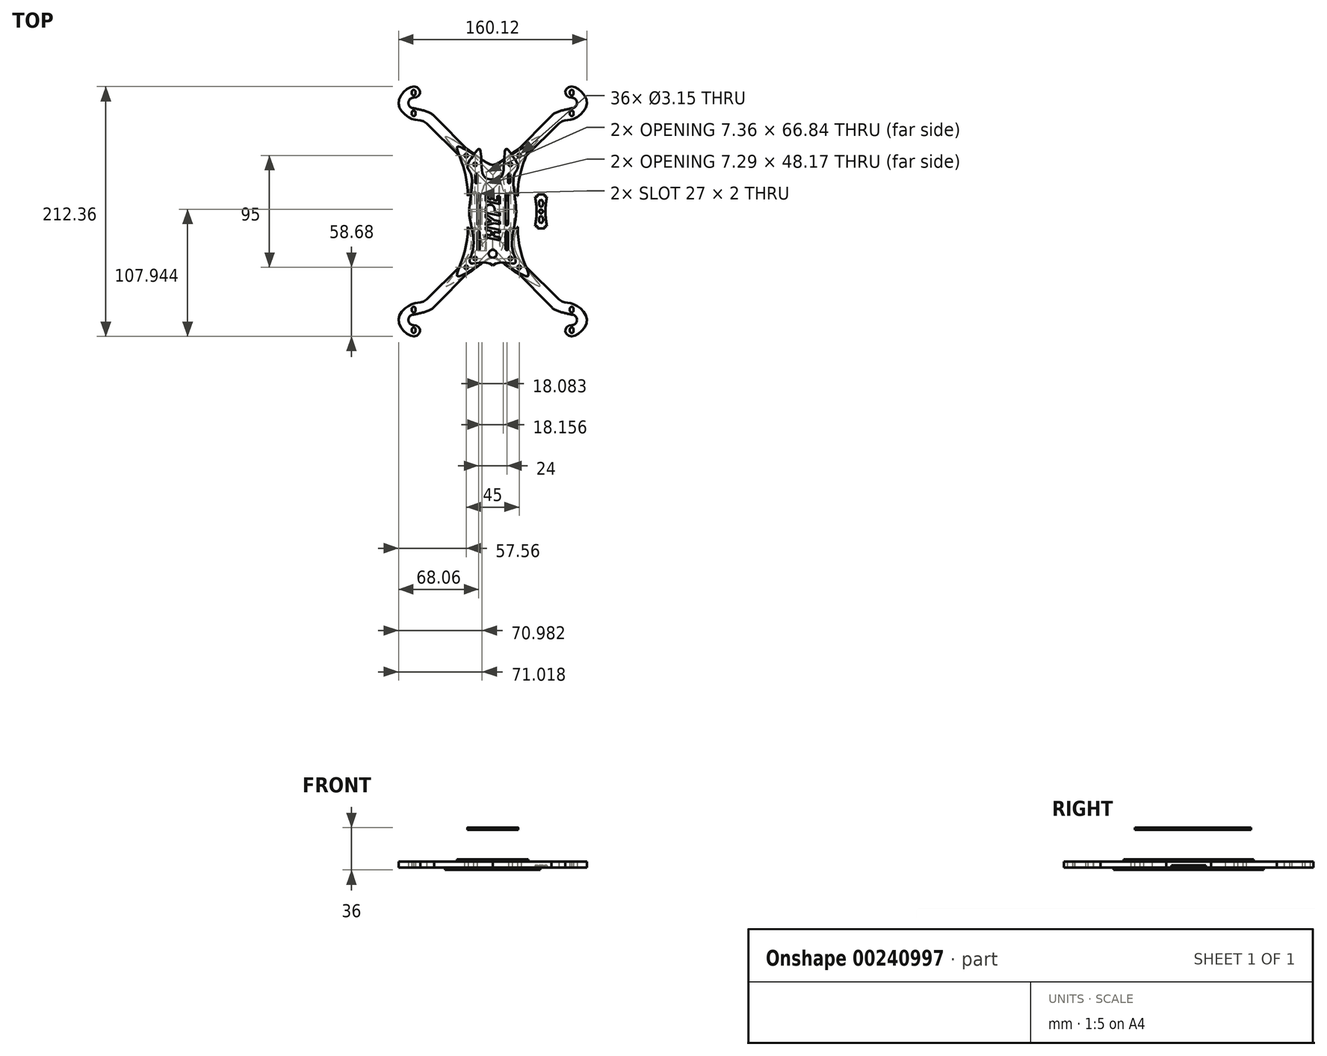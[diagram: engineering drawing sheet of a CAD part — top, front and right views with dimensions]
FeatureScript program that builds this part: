
annotation { "Feature Type Name" : "Feature", "Feature Type Description" : "" }
export const myFeature = defineFeature(function(context is Context, id is Id, definition is map)
    precondition{}
    {
        {
            var Q0;
            Q0=qCreatedBy(makeId("Top.planeOp"),FACE);
            var sketch = newSketch(context, id + "F0", { "sketchPlane" : qUnion([Q0])});
            skLineSegment(sketch, "E0.bottom", {"start": v(15.25, 15.25) * mm, "end": v(-15.25, 15.25) * mm, "construction": true});
            skLineSegment(sketch, "E0.top", {"start": v(15.25, -15.25) * mm, "end": v(-15.25, -15.25) * mm, "construction": true});
            skLineSegment(sketch, "E0.left", {"start": v(15.25, 15.25) * mm, "end": v(15.25, -15.25) * mm, "construction": true});
            skLineSegment(sketch, "E0.right", {"start": v(-15.25, 15.25) * mm, "end": v(-15.25, -15.25) * mm, "construction": true});
            skPoint(sketch, "E0.middle", {"position": v(0, 0) * mm});
            skCircle(sketch, "E1", {"center": v(15.25, 15.25) * mm, "radius": 1.57 * mm});
            skCircle(sketch, "E2", {"center": v(-15.25, 15.25) * mm, "radius": 1.57 * mm});
            skCircle(sketch, "E3", {"center": v(-15.25, -15.25) * mm, "radius": 1.57 * mm});
            skCircle(sketch, "E4", {"center": v(15.25, -15.25) * mm, "radius": 1.57 * mm});
            skLineSegment(sketch, "E5", {"start": v(0, 25) * mm, "end": v(0, -25) * mm, "construction": true});
            skLineSegment(sketch, "E6", {"start": v(0, 25) * mm, "end": v(67.18, 92.18) * mm, "construction": true});
            skLineSegment(sketch, "E7", {"start": v(-57.6, 0) * mm, "end": v(85.6, 0) * mm, "construction": true});
            skLineSegment(sketch, "E8.MirrorCS", {"start": v(0, -25) * mm, "end": v(67.18, -92.18) * mm, "construction": true});
            skLineSegment(sketch, "E9.MirrorCS", {"start": v(0, 25) * mm, "end": v(-67.18, 92.18) * mm, "construction": true});
            skLineSegment(sketch, "E10.MirrorCS", {"start": v(0, -25) * mm, "end": v(-67.18, -92.18) * mm, "construction": true});
            skCircle(sketch, "E11", {"center": v(67.18, 92.18) * mm, "radius": 64.77 * mm, "construction": true});
            skCircle(sketch, "E12", {"center": v(-67.18, 92.18) * mm, "radius": 64.77 * mm, "construction": true});
            skCircle(sketch, "E13", {"center": v(-67.18, -92.18) * mm, "radius": 64.77 * mm, "construction": true});
            skCircle(sketch, "E14", {"center": v(67.18, -92.18) * mm, "radius": 64.77 * mm, "construction": true});
            skLineSegment(sketch, "E15.bottom", {"start": v(18, 18) * mm, "end": v(-18, 18) * mm, "construction": true});
            skLineSegment(sketch, "E15.top", {"start": v(18, -18) * mm, "end": v(-18, -18) * mm, "construction": true});
            skLineSegment(sketch, "E15.left", {"start": v(18, 18) * mm, "end": v(18, -18) * mm, "construction": true});
            skLineSegment(sketch, "E15.right", {"start": v(-18, 18) * mm, "end": v(-18, -18) * mm, "construction": true});
            skSolve(sketch);
        }
        {
            var Q0;
            Q0=qCreatedBy(makeId("Top.planeOp"),FACE);
            var sketch = newSketch(context, id + "F1", { "sketchPlane" : qUnion([Q0])});
            skLineSegment(sketch, "E16.0", {"start": v(0, 25) * mm, "end": v(67.18, 92.18) * mm, "construction": true});
            skLineSegment(sketch, "E16.1", {"start": v(0, 25) * mm, "end": v(-67.18, 92.18) * mm, "construction": true});
            skLineSegment(sketch, "E16.2", {"start": v(0, 25) * mm, "end": v(0, -25) * mm, "construction": true});
            skLineSegment(sketch, "E16.3", {"start": v(0, -25) * mm, "end": v(67.18, -92.18) * mm, "construction": true});
            skLineSegment(sketch, "E16.4", {"start": v(0, -25) * mm, "end": v(-67.18, -92.18) * mm, "construction": true});
            skCircle(sketch, "E17", {"center": v(67.18, 92.18) * mm, "radius": 9.5 * mm, "construction": true});
            skCircle(sketch, "E18", {"center": v(67.18, 92.18) * mm, "radius": 8 * mm, "construction": true});
            skArc(sketch, "E19", {"start": v(67.18, 87.68) * mm, "mid": v(71.68, 92.18) * mm, "end": v(67.18, 96.68) * mm});
            skCircle(sketch, "E20", {"center": v(67.18, 92.18) * mm, "radius": 14 * mm, "construction": true});
            skLineSegment(sketch, "E21", {"start": v(67.18, 92.18) * mm, "end": v(85, 110) * mm, "construction": true});
            skLineSegment(sketch, "E22", {"start": v(52.08, 107.27) * mm, "end": v(67.18, 92.18) * mm, "construction": true});
            skLineSegment(sketch, "E23", {"start": v(67.18, 92.18) * mm, "end": v(82.27, 77.08) * mm, "construction": true});
            skLineSegment(sketch, "E24", {"start": v(67.18, 67.97) * mm, "end": v(67.18, 92.18) * mm, "construction": true});
            skLineSegment(sketch, "E25", {"start": v(67.18, 115.7) * mm, "end": v(67.18, 92.18) * mm, "construction": true});
            skLineSegment(sketch, "E26", {"start": v(42.73, 92.18) * mm, "end": v(67.18, 92.18) * mm, "construction": true});
            skLineSegment(sketch, "E27", {"start": v(96.59, 92.18) * mm, "end": v(67.18, 92.18) * mm, "construction": true});
            skLineSegment(sketch, "E28", {"start": v(67.18, 100.18) * mm, "end": v(67.18, 101.68) * mm, "construction": true});
            skArc(sketch, "E29.0.startCap", {"start": v(68.75, 100.18) * mm, "mid": v(67.18, 98.6) * mm, "end": v(65.6, 100.18) * mm});
            skArc(sketch, "E29.0.endCap", {"start": v(65.6, 101.68) * mm, "mid": v(67.18, 103.25) * mm, "end": v(68.75, 101.68) * mm});
            skLineSegment(sketch, "E29.0.left", {"start": v(65.6, 100.18) * mm, "end": v(65.6, 101.68) * mm});
            skLineSegment(sketch, "E29.0.right", {"start": v(68.75, 100.18) * mm, "end": v(68.75, 101.68) * mm});
            skLineSegment(sketch, "E30", {"start": v(49.85, 81.21) * mm, "end": v(53.03, 78.03) * mm, "construction": true});
            skLineSegment(sketch, "E31", {"start": v(53.03, 78.03) * mm, "end": v(56.21, 74.85) * mm, "construction": true});
            skLineSegment(sketch, "E32", {"start": v(0, 25) * mm, "end": v(0, 53.5) * mm, "construction": true});
            skLineSegment(sketch, "E33", {"start": v(0, -25) * mm, "end": v(0, -52.13) * mm, "construction": true});
            skPoint(sketch, "E34", {"position": v(67.18, 80.07) * mm});
            skLineSegment(sketch, "E35", {"start": v(0, 31) * mm, "end": v(0, 19) * mm});
            skArc(sketch, "E36.MirrorCS", {"start": v(65.6, 82.68) * mm, "mid": v(67.18, 81.1) * mm, "end": v(68.75, 82.68) * mm});
            skLineSegment(sketch, "E37.MirrorCS", {"start": v(68.75, 84.18) * mm, "end": v(68.75, 82.68) * mm});
            skLineSegment(sketch, "E38.MirrorCS", {"start": v(65.6, 84.18) * mm, "end": v(65.6, 82.68) * mm});
            skArc(sketch, "E39.MirrorCS", {"start": v(68.75, 84.18) * mm, "mid": v(67.18, 85.75) * mm, "end": v(65.6, 84.18) * mm});
            skFitSpline(sketch, "E40", {"points": [v(67.18, 87.68) * mm, v(49.85, 81.21) * mm], "startDerivative": vector(-16.97, -3.47) * mm, "endDerivative": vector(-9.2, -10.93) * mm});
            skFitSpline(sketch, "E41", {"points": [v(56.21, 74.85) * mm, v(67.18, 78.18) * mm, v(80.06, 92.18) * mm, v(67.18, 106.18) * mm, v(61.64, 101) * mm, v(67.18, 96.68) * mm], "startDerivative": vector(71.32, 56.31) * mm, "endDerivative": vector(56.06, 0.47) * mm});
            skPoint(sketch, "E42", {"position": v(81.88, 92.18) * mm});
            skLineSegment(sketch, "E43.MirrorCS", {"start": v(-67.18, 100.18) * mm, "end": v(-67.18, 101.68) * mm, "construction": true});
            skLineSegment(sketch, "E44.MirrorCS", {"start": v(-49.85, 81.21) * mm, "end": v(-53.03, 78.03) * mm, "construction": true});
            skLineSegment(sketch, "E45.MirrorCS", {"start": v(-53.03, 78.03) * mm, "end": v(-56.21, 74.85) * mm, "construction": true});
            skLineSegment(sketch, "E46.MirrorCS", {"start": v(-42.73, 92.18) * mm, "end": v(-67.18, 92.18) * mm, "construction": true});
            skLineSegment(sketch, "E47.MirrorCS", {"start": v(-67.18, 92.18) * mm, "end": v(-85, 110) * mm, "construction": true});
            skCircle(sketch, "E48.MirrorC", {"center": v(-67.18, 92.18) * mm, "radius": 14 * mm, "construction": true});
            skLineSegment(sketch, "E49.MirrorCS", {"start": v(-67.18, 67.97) * mm, "end": v(-67.18, 92.18) * mm, "construction": true});
            skLineSegment(sketch, "E50.MirrorCS", {"start": v(-67.18, 115.7) * mm, "end": v(-67.18, 92.18) * mm, "construction": true});
            skCircle(sketch, "E51.MirrorC", {"center": v(-67.18, 92.18) * mm, "radius": 8 * mm, "construction": true});
            skLineSegment(sketch, "E52.MirrorCS", {"start": v(-96.59, 92.18) * mm, "end": v(-67.18, 92.18) * mm, "construction": true});
            skCircle(sketch, "E53.MirrorC", {"center": v(-67.18, 92.18) * mm, "radius": 9.5 * mm, "construction": true});
            skPoint(sketch, "E54.MirrorP", {"position": v(-81.88, 92.18) * mm});
            skLineSegment(sketch, "E55.MirrorCS", {"start": v(-52.08, 107.27) * mm, "end": v(-67.18, 92.18) * mm, "construction": true});
            skLineSegment(sketch, "E56.MirrorCS", {"start": v(-67.18, 92.18) * mm, "end": v(-82.27, 77.08) * mm, "construction": true});
            skPoint(sketch, "E57.MirrorP", {"position": v(-67.18, 80.07) * mm});
            skLineSegment(sketch, "E58.MirrorCS", {"start": v(-67.18, -100.18) * mm, "end": v(-67.18, -101.68) * mm, "construction": true});
            skLineSegment(sketch, "E59.MirrorCS", {"start": v(53.03, -78.03) * mm, "end": v(56.21, -74.85) * mm, "construction": true});
            skLineSegment(sketch, "E60.MirrorCS", {"start": v(-53.03, -78.03) * mm, "end": v(-56.21, -74.85) * mm, "construction": true});
            skLineSegment(sketch, "E61.MirrorCS", {"start": v(-49.85, -81.21) * mm, "end": v(-53.03, -78.03) * mm, "construction": true});
            skLineSegment(sketch, "E62.MirrorCS", {"start": v(49.85, -81.21) * mm, "end": v(53.03, -78.03) * mm, "construction": true});
            skLineSegment(sketch, "E63.MirrorCS", {"start": v(67.18, -100.18) * mm, "end": v(67.18, -101.68) * mm, "construction": true});
            skLineSegment(sketch, "E64.MirrorCS", {"start": v(-52.08, -107.27) * mm, "end": v(-67.18, -92.18) * mm, "construction": true});
            skLineSegment(sketch, "E65.MirrorCS", {"start": v(67.18, -67.97) * mm, "end": v(67.18, -92.18) * mm, "construction": true});
            skLineSegment(sketch, "E66.MirrorCS", {"start": v(52.08, -107.27) * mm, "end": v(67.18, -92.18) * mm, "construction": true});
            skLineSegment(sketch, "E67.MirrorCS", {"start": v(-67.18, -92.18) * mm, "end": v(-82.27, -77.08) * mm, "construction": true});
            skLineSegment(sketch, "E68.MirrorCS", {"start": v(-67.18, -67.97) * mm, "end": v(-67.18, -92.18) * mm, "construction": true});
            skLineSegment(sketch, "E69.MirrorCS", {"start": v(42.73, -92.18) * mm, "end": v(67.18, -92.18) * mm, "construction": true});
            skLineSegment(sketch, "E70.MirrorCS", {"start": v(-67.18, -115.7) * mm, "end": v(-67.18, -92.18) * mm, "construction": true});
            skLineSegment(sketch, "E71.MirrorCS", {"start": v(-42.73, -92.18) * mm, "end": v(-67.18, -92.18) * mm, "construction": true});
            skLineSegment(sketch, "E72.MirrorCS", {"start": v(67.18, -115.7) * mm, "end": v(67.18, -92.18) * mm, "construction": true});
            skPoint(sketch, "E73.MirrorP", {"position": v(81.88, -92.18) * mm});
            skCircle(sketch, "E74.MirrorC", {"center": v(-67.18, -92.18) * mm, "radius": 8 * mm, "construction": true});
            skLineSegment(sketch, "E75.MirrorCS", {"start": v(67.18, -92.18) * mm, "end": v(82.27, -77.08) * mm, "construction": true});
            skLineSegment(sketch, "E76.MirrorCS", {"start": v(67.18, -92.18) * mm, "end": v(85, -110) * mm, "construction": true});
            skCircle(sketch, "E77.MirrorC", {"center": v(67.18, -92.18) * mm, "radius": 14 * mm, "construction": true});
            skCircle(sketch, "E78.MirrorC", {"center": v(67.18, -92.18) * mm, "radius": 8 * mm, "construction": true});
            skPoint(sketch, "E79.MirrorP", {"position": v(-81.88, -92.18) * mm});
            skPoint(sketch, "E80.MirrorP", {"position": v(67.18, -80.07) * mm});
            skLineSegment(sketch, "E81.MirrorCS", {"start": v(-67.18, -92.18) * mm, "end": v(-85, -110) * mm, "construction": true});
            skCircle(sketch, "E82.MirrorC", {"center": v(-67.18, -92.18) * mm, "radius": 14 * mm, "construction": true});
            skCircle(sketch, "E83.MirrorC", {"center": v(-67.18, -92.18) * mm, "radius": 9.5 * mm, "construction": true});
            skPoint(sketch, "E84.MirrorP", {"position": v(-67.18, -80.07) * mm});
            skLineSegment(sketch, "E85.MirrorCS", {"start": v(-96.59, -92.18) * mm, "end": v(-67.18, -92.18) * mm, "construction": true});
            skLineSegment(sketch, "E86.MirrorCS", {"start": v(96.59, -92.18) * mm, "end": v(67.18, -92.18) * mm, "construction": true});
            skCircle(sketch, "E87.MirrorC", {"center": v(67.18, -92.18) * mm, "radius": 9.5 * mm, "construction": true});
            skLineSegment(sketch, "E88.bottom", {"start": v(22.5, 47.5) * mm, "end": v(-22.5, 47.5) * mm, "construction": true});
            skLineSegment(sketch, "E88.top", {"start": v(22.5, -47.5) * mm, "end": v(-22.5, -47.5) * mm, "construction": true});
            skLineSegment(sketch, "E88.left", {"start": v(22.5, 47.5) * mm, "end": v(22.5, -47.5) * mm, "construction": true});
            skLineSegment(sketch, "E88.right", {"start": v(-22.5, 47.5) * mm, "end": v(-22.5, -47.5) * mm, "construction": true});
            skPoint(sketch, "E88.middle", {"position": v(0, 0) * mm});
            skLineSegment(sketch, "E89.bottom", {"start": v(15, 40) * mm, "end": v(-15, 40) * mm, "construction": true});
            skLineSegment(sketch, "E89.top", {"start": v(15, -40) * mm, "end": v(-15, -40) * mm, "construction": true});
            skLineSegment(sketch, "E89.left", {"start": v(15, 40) * mm, "end": v(15, -40) * mm, "construction": true});
            skLineSegment(sketch, "E89.right", {"start": v(-15, 40) * mm, "end": v(-15, -40) * mm, "construction": true});
            skCircle(sketch, "E90", {"center": v(22.5, 47.5) * mm, "radius": 1.57 * mm});
            skCircle(sketch, "E91", {"center": v(15, 40) * mm, "radius": 1.57 * mm});
            skCircle(sketch, "E92", {"center": v(-22.5, 47.5) * mm, "radius": 1.57 * mm, "construction": true});
            skCircle(sketch, "E93", {"center": v(-15, 40) * mm, "radius": 1.57 * mm, "construction": true});
            skCircle(sketch, "E94", {"center": v(22.5, -47.5) * mm, "radius": 1.57 * mm, "construction": true});
            skCircle(sketch, "E95", {"center": v(15, -40) * mm, "radius": 1.57 * mm, "construction": true});
            skCircle(sketch, "E96", {"center": v(-15, -40) * mm, "radius": 1.57 * mm, "construction": true});
            skCircle(sketch, "E97", {"center": v(-22.5, -47.5) * mm, "radius": 1.57 * mm, "construction": true});
            skLineSegment(sketch, "E98", {"start": v(49.85, 81.21) * mm, "end": v(0, 31) * mm});
            skLineSegment(sketch, "E99", {"start": v(56.21, 74.85) * mm, "end": v(0, 19) * mm});
            skSolve(sketch);
        }
        {
            var Q0;
            Q0 = qSketchRegion(id + "F1", true);
            extrude(context, id + "F2", {"entities" : qUnion([Q0]), "depth" : 5 * mm});
        }
        {
            var Q0;
            Q0=qCreatedBy(makeId("Top.planeOp"),FACE);
            cPlane(context, id + "F3", {"entities" : qUnion([Q0]), "cplaneType" : CPlaneType.OFFSET, "offset" : 5 * mm, "width" : 150 * mm, "height" : 150 * mm});
        }
        {
            var Q0;
            Q0=qCreatedBy(id+"F3.planeOp",FACE);
            var sketch = newSketch(context, id + "F4", { "sketchPlane" : qUnion([Q0])});
            skLineSegment(sketch, "E100", {"start": v(0, 93.49) * mm, "end": v(0, -92.27) * mm, "construction": true});
            skLineSegment(sketch, "E101", {"start": v(98.9, 0) * mm, "end": v(-102.09, 0) * mm, "construction": true});
            skCircle(sketch, "E102.0", {"center": v(22.5, 47.5) * mm, "radius": 1.57 * mm});
            skCircle(sketch, "E102.1", {"center": v(15, 40) * mm, "radius": 1.57 * mm});
            skCircle(sketch, "E102.2", {"center": v(-15, 40) * mm, "radius": 1.57 * mm});
            skCircle(sketch, "E102.3", {"center": v(-22.5, 47.5) * mm, "radius": 1.57 * mm});
            skCircle(sketch, "E102.4", {"center": v(15.25, 15.25) * mm, "radius": 1.57 * mm});
            skCircle(sketch, "E102.5", {"center": v(15.25, -15.25) * mm, "radius": 1.57 * mm});
            skCircle(sketch, "E102.6", {"center": v(-15.25, -15.25) * mm, "radius": 1.57 * mm});
            skCircle(sketch, "E102.7", {"center": v(-15.25, 15.25) * mm, "radius": 1.57 * mm});
            skCircle(sketch, "E102.8", {"center": v(15, -40) * mm, "radius": 1.57 * mm});
            skCircle(sketch, "E102.9", {"center": v(22.5, -47.5) * mm, "radius": 1.57 * mm});
            skCircle(sketch, "E102.10", {"center": v(-15, -40) * mm, "radius": 1.57 * mm});
            skCircle(sketch, "E102.11", {"center": v(-22.5, -47.5) * mm, "radius": 1.57 * mm});
            skLineSegment(sketch, "E103", {"start": v(-14, 28) * mm, "end": v(0, 28) * mm, "construction": true});
            skLineSegment(sketch, "E104", {"start": v(0, 28) * mm, "end": v(14, 28) * mm, "construction": true});
            skLineSegment(sketch, "E105", {"start": v(19.6, 13.2) * mm, "end": v(19.6, -13.2) * mm, "construction": true});
            skPoint(sketch, "E106", {"position": v(19.6, 0) * mm});
            skArc(sketch, "E107.0.startCap", {"start": v(18.03, 13.2) * mm, "mid": v(19.6, 14.78) * mm, "end": v(21.18, 13.2) * mm});
            skArc(sketch, "E107.0.endCap", {"start": v(21.18, -13.2) * mm, "mid": v(19.6, -14.78) * mm, "end": v(18.03, -13.2) * mm});
            skLineSegment(sketch, "E107.0.right", {"start": v(18.03, 13.2) * mm, "end": v(18.03, -13.2) * mm});
            skLineSegment(sketch, "E108", {"start": v(0, 28) * mm, "end": v(0, 53) * mm, "construction": true});
            skLineSegment(sketch, "E109.0", {"start": v(0, 25) * mm, "end": v(67.18, 92.18) * mm, "construction": true});
            skLineSegment(sketch, "E109.1", {"start": v(0, -25) * mm, "end": v(67.18, -92.18) * mm, "construction": true});
            skFitSpline(sketch, "E110", {"points": [v(0, 39.63) * mm, v(13.42, 46.83) * mm, v(29.94, 54.94) * mm, v(21.18, 13.2) * mm], "startDerivative": vector(29.1, -3) * mm, "endDerivative": vector(1.25, -163.46) * mm});
            skFitSpline(sketch, "E111.MirrorCS", {"points": [v(0, -39.63) * mm, v(13.42, -46.83) * mm, v(29.94, -54.94) * mm, v(21.18, -13.2) * mm], "startDerivative": vector(29.1, 3) * mm, "endDerivative": vector(1.25, 163.46) * mm});
            skFitSpline(sketch, "E112", {"points": [v(5.6, 0) * mm, v(6.14, 24.09) * mm, v(12.72, 0) * mm], "startDerivative": vector(2.53, 34.66) * mm, "endDerivative": vector(0.97, -32.1) * mm});
            skFitSpline(sketch, "E113.MirrorCS", {"points": [v(5.6, 0) * mm, v(6.14, -24.09) * mm, v(12.72, 0) * mm], "startDerivative": vector(2.53, -34.66) * mm, "endDerivative": vector(0.97, 32.1) * mm});
            skFitSpline(sketch, "E114.MirrorCS", {"points": [v(0, 39.63) * mm, v(-13.42, 46.83) * mm, v(-29.94, 54.94) * mm, v(-21.18, 13.2) * mm], "startDerivative": vector(-29.1, -3) * mm, "endDerivative": vector(-1.25, -163.46) * mm});
            skFitSpline(sketch, "E115.MirrorCS", {"points": [v(-5.6, 0) * mm, v(-6.14, 24.09) * mm, v(-12.72, 0) * mm], "startDerivative": vector(-2.53, 34.66) * mm, "endDerivative": vector(-0.97, -32.1) * mm});
            skFitSpline(sketch, "E116.MirrorCS", {"points": [v(-5.6, 0) * mm, v(-6.14, -24.09) * mm, v(-12.72, 0) * mm], "startDerivative": vector(-2.53, -34.66) * mm, "endDerivative": vector(-0.97, 32.1) * mm});
            skLineSegment(sketch, "E117.MirrorCS", {"start": v(-18.03, 13.2) * mm, "end": v(-18.03, -13.2) * mm});
            skArc(sketch, "E118.MirrorCS", {"start": v(-18.03, 13.2) * mm, "mid": v(-19.6, 14.78) * mm, "end": v(-21.18, 13.2) * mm});
            skArc(sketch, "E119.MirrorCS", {"start": v(-21.18, -13.2) * mm, "mid": v(-19.6, -14.78) * mm, "end": v(-18.03, -13.2) * mm});
            skFitSpline(sketch, "E120.MirrorCS", {"points": [v(0, -39.63) * mm, v(-13.42, -46.83) * mm, v(-29.94, -54.94) * mm, v(-21.18, -13.2) * mm], "startDerivative": vector(-29.1, 3) * mm, "endDerivative": vector(-1.25, 163.46) * mm});
            skLineSegment(sketch, "E121", {"start": v(14, 25) * mm, "end": v(14, 31) * mm, "construction": true});
            skArc(sketch, "E122.0.startCap", {"start": v(15, 25) * mm, "mid": v(14, 24) * mm, "end": v(13, 25) * mm});
            skArc(sketch, "E122.0.endCap", {"start": v(13, 31) * mm, "mid": v(14, 32) * mm, "end": v(15, 31) * mm});
            skLineSegment(sketch, "E122.0.left", {"start": v(13, 25) * mm, "end": v(13, 31) * mm});
            skLineSegment(sketch, "E122.0.right", {"start": v(15, 25) * mm, "end": v(15, 31) * mm});
            skLineSegment(sketch, "E123.MirrorCS", {"start": v(-15, 25) * mm, "end": v(-15, 31) * mm});
            skLineSegment(sketch, "E124.MirrorCS", {"start": v(-13, 25) * mm, "end": v(-13, 31) * mm});
            skArc(sketch, "E125.MirrorCS", {"start": v(-15, 25) * mm, "mid": v(-14, 24) * mm, "end": v(-13, 25) * mm});
            skArc(sketch, "E126.MirrorCS", {"start": v(-13, 31) * mm, "mid": v(-14, 32) * mm, "end": v(-15, 31) * mm});
            skSolve(sketch);
        }
        {
            var Q0;
            Q0=makeQuery(id+"F4.imprint","IMPRINT",FACE,{"disambiguationData":[TD([[makeQuery(id+"F4.imprint","IMPRINT",EDGE,{"derivedFrom":sQuery(id+"F4.wireOp",EDGE,"E102.0")}),-1.0]])]});
            extrude(context, id + "F5", {"entities" : qUnion([Q0]), "depth" : 2 * mm});
        }
        {
            var Q0;
            Q0=qCreatedBy(makeId("Top.planeOp"),FACE);
            var sketch = newSketch(context, id + "F6", { "sketchPlane" : qUnion([Q0])});
            skFitSpline(sketch, "E127.0.0", {"points": [v(-21.18, -13.2) * mm, v(-21, -37.37) * mm, v(-40.42, -63.57) * mm, v(-12.7, -46.72) * mm, v(-2.57, -39.37) * mm, v(0, -39.63) * mm]});
            skFitSpline(sketch, "E127.0.1", {"points": [v(0, -39.63) * mm, v(2.57, -39.37) * mm, v(12.7, -46.72) * mm, v(40.42, -63.57) * mm, v(21, -37.37) * mm, v(21.18, -13.2) * mm]});
            skArc(sketch, "E127.0.2", {"start": v(21.18, -13.2) * mm, "mid": v(19.6, -14.78) * mm, "end": v(18.03, -13.2) * mm});
            skLineSegment(sketch, "E127.0.3", {"start": v(18.03, -13.2) * mm, "end": v(18.03, 13.2) * mm});
            skArc(sketch, "E127.0.4", {"start": v(18.03, 13.2) * mm, "mid": v(19.6, 14.78) * mm, "end": v(21.18, 13.2) * mm});
            skFitSpline(sketch, "E127.0.5", {"points": [v(21.18, 13.2) * mm, v(21, 37.37) * mm, v(40.42, 63.57) * mm, v(12.7, 46.72) * mm, v(2.57, 39.37) * mm, v(0, 39.63) * mm]});
            skFitSpline(sketch, "E127.0.6", {"points": [v(0, 39.63) * mm, v(-2.57, 39.37) * mm, v(-12.7, 46.72) * mm, v(-40.42, 63.57) * mm, v(-21, 37.37) * mm, v(-21.18, 13.2) * mm]});
            skArc(sketch, "E127.0.7", {"start": v(-21.18, 13.2) * mm, "mid": v(-19.6, 14.78) * mm, "end": v(-18.03, 13.2) * mm});
            skLineSegment(sketch, "E127.0.8", {"start": v(-18.03, 13.2) * mm, "end": v(-18.03, -13.2) * mm});
            skArc(sketch, "E127.0.9", {"start": v(-18.03, -13.2) * mm, "mid": v(-19.6, -14.78) * mm, "end": v(-21.18, -13.2) * mm});
            skFitSpline(sketch, "E128.0.0", {"points": [v(12.72, 0) * mm, v(12.56, 5.38) * mm, v(7, 33.42) * mm, v(5.38, 4.53) * mm, v(5.6, 0) * mm]});
            skFitSpline(sketch, "E128.0.1", {"points": [v(5.6, 0) * mm, v(5.38, -4.53) * mm, v(7, -33.42) * mm, v(12.56, -5.38) * mm, v(12.72, 0) * mm]});
            skFitSpline(sketch, "E128.1.0", {"points": [v(-12.72, 0) * mm, v(-12.56, -5.38) * mm, v(-7, -33.42) * mm, v(-5.38, -4.53) * mm, v(-5.6, 0) * mm]});
            skFitSpline(sketch, "E128.1.1", {"points": [v(-5.6, 0) * mm, v(-5.38, 4.53) * mm, v(-7, 33.42) * mm, v(-12.56, 5.38) * mm, v(-12.72, 0) * mm]});
            skCircle(sketch, "E128.2", {"center": v(15.25, 15.25) * mm, "radius": 1.57 * mm});
            skCircle(sketch, "E128.3", {"center": v(15, 40) * mm, "radius": 1.57 * mm});
            skCircle(sketch, "E128.4", {"center": v(-15, 40) * mm, "radius": 1.57 * mm});
            skCircle(sketch, "E128.5", {"center": v(-15.25, 15.25) * mm, "radius": 1.57 * mm});
            skCircle(sketch, "E128.6", {"center": v(-15.25, -15.25) * mm, "radius": 1.57 * mm});
            skCircle(sketch, "E128.7", {"center": v(15.25, -15.25) * mm, "radius": 1.57 * mm});
            skCircle(sketch, "E128.8", {"center": v(15, -40) * mm, "radius": 1.57 * mm});
            skCircle(sketch, "E128.9", {"center": v(22.5, -47.5) * mm, "radius": 1.57 * mm});
            skCircle(sketch, "E128.10", {"center": v(-15, -40) * mm, "radius": 1.57 * mm});
            skCircle(sketch, "E128.11", {"center": v(-22.5, -47.5) * mm, "radius": 1.57 * mm});
            skCircle(sketch, "E128.12", {"center": v(22.5, 47.5) * mm, "radius": 1.57 * mm});
            skCircle(sketch, "E128.13", {"center": v(-22.5, 47.5) * mm, "radius": 1.57 * mm});
            skSolve(sketch);
        }
        {
            var Q0;
            Q0 = qSketchRegion(id + "F6", true);
            extrude(context, id + "F7", {"entities" : qUnion([Q0]), "oppositeDirection" : true, "depth" : 2 * mm});
        }
        {
            var Q0;
            Q0=qCreatedBy(makeId("Top.planeOp"),FACE);
            cPlane(context, id + "F8", {"entities" : qUnion([Q0]), "cplaneType" : CPlaneType.OFFSET, "offset" : 32 * mm, "width" : 150 * mm, "height" : 150 * mm});
        }
        {
            var Q0;
            Q0=qCreatedBy(id+"F8.planeOp",FACE);
            var sketch = newSketch(context, id + "F9", { "sketchPlane" : qUnion([Q0])});
            skCircle(sketch, "E129.0", {"center": v(15, 40) * mm, "radius": 1.57 * mm});
            skCircle(sketch, "E129.1", {"center": v(-15, 40) * mm, "radius": 1.57 * mm});
            skCircle(sketch, "E129.2", {"center": v(-15, -40) * mm, "radius": 1.57 * mm});
            skCircle(sketch, "E129.3", {"center": v(15, -40) * mm, "radius": 1.57 * mm});
            skArc(sketch, "E130.0.0", {"start": v(15, 31) * mm, "mid": v(14, 32) * mm, "end": v(13, 31) * mm});
            skLineSegment(sketch, "E130.0.1", {"start": v(13, 31) * mm, "end": v(13, 25) * mm});
            skArc(sketch, "E130.0.2", {"start": v(13, 25) * mm, "mid": v(14, 24) * mm, "end": v(15, 25) * mm});
            skLineSegment(sketch, "E130.0.3", {"start": v(15, 25) * mm, "end": v(15, 31) * mm});
            skArc(sketch, "E130.1.0", {"start": v(-15, 25) * mm, "mid": v(-14, 24) * mm, "end": v(-13, 25) * mm});
            skLineSegment(sketch, "E130.1.1", {"start": v(-13, 25) * mm, "end": v(-13, 31) * mm});
            skArc(sketch, "E130.1.2", {"start": v(-13, 31) * mm, "mid": v(-14, 32) * mm, "end": v(-15, 31) * mm});
            skLineSegment(sketch, "E130.1.3", {"start": v(-15, 31) * mm, "end": v(-15, 25) * mm});
            skLineSegment(sketch, "E131.0", {"start": v(0, 28) * mm, "end": v(14, 28) * mm, "construction": true});
            skLineSegment(sketch, "E131.1", {"start": v(-14, 28) * mm, "end": v(0, 28) * mm, "construction": true});
            skLineSegment(sketch, "E132", {"start": v(0, 65.45) * mm, "end": v(0, -61.92) * mm, "construction": true});
            skLineSegment(sketch, "E133", {"start": v(64.66, 0) * mm, "end": v(-63.92, 0) * mm, "construction": true});
            skLineSegment(sketch, "E134", {"start": v(0, 39.69) * mm, "end": v(9, 39.69) * mm, "construction": true});
            skLineSegment(sketch, "E135.0", {"start": v(0, 25) * mm, "end": v(67.18, 92.18) * mm, "construction": true});
            skLineSegment(sketch, "E135.1", {"start": v(0, 25) * mm, "end": v(-67.18, 92.18) * mm, "construction": true});
            skLineSegment(sketch, "E135.2", {"start": v(0, -25) * mm, "end": v(67.18, -92.18) * mm, "construction": true});
            skLineSegment(sketch, "E135.3", {"start": v(0, -25) * mm, "end": v(-67.18, -92.18) * mm, "construction": true});
            skLineSegment(sketch, "E136", {"start": v(0, -25) * mm, "end": v(12, -25) * mm, "construction": true});
            skLineSegment(sketch, "E137", {"start": v(0, 1.76) * mm, "end": v(12, 1.76) * mm, "construction": true});
            skLineSegment(sketch, "E138", {"start": v(12, -10.74) * mm, "end": v(12, 14.26) * mm, "construction": true});
            skLineSegment(sketch, "E139", {"start": v(12, -31.96) * mm, "end": v(12, -18.04) * mm, "construction": true});
            skArc(sketch, "E140.0.startCap", {"start": v(13, -31.96) * mm, "mid": v(12, -32.96) * mm, "end": v(11, -31.96) * mm});
            skArc(sketch, "E140.0.endCap", {"start": v(11, -18.04) * mm, "mid": v(12, -17.04) * mm, "end": v(13, -18.04) * mm});
            skLineSegment(sketch, "E140.0.left", {"start": v(11, -31.96) * mm, "end": v(11, -18.04) * mm});
            skLineSegment(sketch, "E140.0.right", {"start": v(13, -31.96) * mm, "end": v(13, -18.04) * mm});
            skArc(sketch, "E141.0.startCap", {"start": v(13, -10.74) * mm, "mid": v(12, -11.74) * mm, "end": v(11, -10.74) * mm});
            skArc(sketch, "E141.0.endCap", {"start": v(11, 14.26) * mm, "mid": v(12, 15.26) * mm, "end": v(13, 14.26) * mm});
            skLineSegment(sketch, "E141.0.left", {"start": v(11, -10.74) * mm, "end": v(11, 14.26) * mm});
            skLineSegment(sketch, "E141.0.right", {"start": v(13, -10.74) * mm, "end": v(13, 14.26) * mm});
            skLineSegment(sketch, "E142.MirrorCS", {"start": v(-13, -10.74) * mm, "end": v(-13, 14.26) * mm});
            skLineSegment(sketch, "E143.MirrorCS", {"start": v(-11, -10.74) * mm, "end": v(-11, 14.26) * mm});
            skArc(sketch, "E144.MirrorCS", {"start": v(-11, 14.26) * mm, "mid": v(-12, 15.26) * mm, "end": v(-13, 14.26) * mm});
            skArc(sketch, "E145.MirrorCS", {"start": v(-13, -10.74) * mm, "mid": v(-12, -11.74) * mm, "end": v(-11, -10.74) * mm});
            skArc(sketch, "E146.MirrorCS", {"start": v(-11, -18.04) * mm, "mid": v(-12, -17.04) * mm, "end": v(-13, -18.04) * mm});
            skLineSegment(sketch, "E147.MirrorCS", {"start": v(-13, -31.96) * mm, "end": v(-13, -18.04) * mm});
            skArc(sketch, "E148.MirrorCS", {"start": v(-13, -31.96) * mm, "mid": v(-12, -32.96) * mm, "end": v(-11, -31.96) * mm});
            skLineSegment(sketch, "E149.MirrorCS", {"start": v(-11, -31.96) * mm, "end": v(-11, -18.04) * mm});
            skCircle(sketch, "E150", {"center": v(0, -36) * mm, "radius": 3.35 * mm});
            skFitSpline(sketch, "E151", {"points": [v(0, 27.08) * mm, v(8.14, 31) * mm, v(11.4, 53.05) * mm, v(19.14, 44.14) * mm], "startDerivative": vector(37.78, 5.14) * mm, "endDerivative": vector(20.69, -22.19) * mm});
            skFitSpline(sketch, "E152", {"points": [v(19.14, 44.14) * mm, v(18.43, 31.84) * mm, v(20, 0) * mm], "startDerivative": vector(38.52, -57.06) * mm, "endDerivative": vector(3, -59.65) * mm});
            skFitSpline(sketch, "E153.MirrorCS", {"points": [v(-19.14, 44.14) * mm, v(-18.43, 31.84) * mm, v(-20, 0) * mm], "startDerivative": vector(-38.52, -57.06) * mm, "endDerivative": vector(-3, -59.65) * mm});
            skFitSpline(sketch, "E154.MirrorCS", {"points": [v(0, 27.08) * mm, v(-8.14, 31) * mm, v(-11.4, 53.05) * mm, v(-19.14, 44.14) * mm], "startDerivative": vector(-37.78, 5.14) * mm, "endDerivative": vector(-20.69, -22.19) * mm});
            skFitSpline(sketch, "E155", {"points": [v(20, 0) * mm, v(16.55, -30.79) * mm, v(18.91, -43.91) * mm, v(0, -45.78) * mm], "startDerivative": vector(-1.47, -76.62) * mm, "endDerivative": vector(-52.88, -46.97) * mm});
            skFitSpline(sketch, "E156.MirrorCS", {"points": [v(-20, 0) * mm, v(-16.55, -30.79) * mm, v(-18.91, -43.91) * mm, v(0, -45.78) * mm], "startDerivative": vector(1.47, -76.62) * mm, "endDerivative": vector(52.88, -46.97) * mm});
            skText(sketch, "E157", { "text": "HYPE", "fontName": "OpenSans-BoldItalic.ttf"});
            const initialGuessF9  = {"E157": [0.006, -0.025, 0, 1, 0.012]};
            skSetInitialGuess(sketch, initialGuessF9);
            skSolve(sketch);
        }
        {
            var Q0;
            Q0 = qSketchRegion(id + "F9", true);
            extrude(context, id + "F10", {"entities" : qUnion([Q0]), "depth" : 2 * mm});
        }
        {
            var Q0;
            Q0=sQuery(id+"F4.wireOp",EDGE,"E102.1");
            var Q1;
            Q1=sQuery(id+"F4.wireOp",EDGE,"E102.2");
            var Q2;
            Q2=sQuery(id+"F4.wireOp",EDGE,"E102.10");
            var Q3;
            Q3=sQuery(id+"F4.wireOp",EDGE,"E102.8");
            extrude(context, id + "F11", {"bodyType" : ToolBodyType.SURFACE, "surfaceEntities" : qUnion([Q0, Q1, Q2, Q3]), "depth" : 27 * mm});
        }
        {
            var Q0;
            Q0=qCreatedBy(makeId("Top.planeOp"),FACE);
            var sketch = newSketch(context, id + "F12", { "sketchPlane" : qUnion([Q0])});
            skLineSegment(sketch, "E158", {"start": v(-21.46, 0) * mm, "end": v(41.07, 0) * mm, "construction": true});
            skLineSegment(sketch, "E159.bottom", {"start": v(46.07, 12.5) * mm, "end": v(44.07, 12.5) * mm});
            skLineSegment(sketch, "E159.top", {"start": v(46.07, -12.5) * mm, "end": v(36.07, -12.5) * mm, "construction": true});
            skLineSegment(sketch, "E159.left", {"start": v(46.07, 12.5) * mm, "end": v(46.07, -12.5) * mm, "construction": true});
            skLineSegment(sketch, "E159.right", {"start": v(36.07, 12.5) * mm, "end": v(36.07, -12.5) * mm, "construction": true});
            skPoint(sketch, "E159.middle", {"position": v(41.07, 0) * mm});
            skLineSegment(sketch, "E160", {"start": v(41.07, 19.81) * mm, "end": v(41.07, -21.3) * mm, "construction": true});
            skCircle(sketch, "E161", {"center": v(41.07, 0) * mm, "radius": 1.6 * mm});
            skEllipse(sketch, "E162", {"center": v(41.07, 6.88) * mm, "majorRadius": 3 * mm, "minorRadius": 1.75 * mm, "majorAxis": v(0, 1)});
            skEllipse(sketch, "E163.MirrorC", {"center": v(41.07, -6.88) * mm, "majorRadius": 3 * mm, "minorRadius": 1.75 * mm, "majorAxis": v(0, -1)});
            skFitSpline(sketch, "E164", {"points": [v(46.07, 12.5) * mm, v(44.8, 0) * mm, v(46.07, -12.5) * mm], "startDerivative": vector(-4.03, -25) * mm, "endDerivative": vector(4.03, -25) * mm});
            skFitSpline(sketch, "E165.MirrorCS", {"points": [v(36.07, 12.5) * mm, v(37.32, 0) * mm, v(36.07, -12.5) * mm], "startDerivative": vector(4.03, -25) * mm, "endDerivative": vector(-4.03, -25) * mm});
            skLineSegment(sketch, "E166", {"start": v(38.07, 14.5) * mm, "end": v(41.07, 14.5) * mm});
            skLineSegment(sketch, "E167", {"start": v(41.07, 14.5) * mm, "end": v(44.07, 14.5) * mm});
            skLineSegment(sketch, "E168", {"start": v(44.07, 14.5) * mm, "end": v(44.07, 12.5) * mm});
            skLineSegment(sketch, "E169", {"start": v(38.07, 14.5) * mm, "end": v(38.07, 12.5) * mm});
            skLineSegment(sketch, "E170.trimOffspring", {"start": v(38.07, 12.5) * mm, "end": v(36.07, 12.5) * mm});
            skLineSegment(sketch, "E171.MirrorCS", {"start": v(41.07, -14.5) * mm, "end": v(44.07, -14.5) * mm});
            skLineSegment(sketch, "E172.MirrorCS", {"start": v(38.07, -14.5) * mm, "end": v(41.07, -14.5) * mm});
            skLineSegment(sketch, "E173.MirrorCS", {"start": v(38.07, -12.5) * mm, "end": v(36.07, -12.5) * mm});
            skLineSegment(sketch, "E174.MirrorCS", {"start": v(46.07, -12.5) * mm, "end": v(44.07, -12.5) * mm});
            skLineSegment(sketch, "E175.MirrorCS", {"start": v(44.07, -14.5) * mm, "end": v(44.07, -12.5) * mm});
            skLineSegment(sketch, "E176.MirrorCS", {"start": v(38.07, -14.5) * mm, "end": v(38.07, -12.5) * mm});
            skSolve(sketch);
        }
        {
            var Q0;
            Q0=makeQuery(id+"F12.imprint","IMPRINT",FACE,{"disambiguationData":[TD([[makeQuery(id+"F12.imprint","IMPRINT",EDGE,{"derivedFrom":sQuery(id+"F12.wireOp",EDGE,"E159.bottom")}),1.0]])]});
            extrude(context, id + "F13", {"entities" : qUnion([Q0]), "depth" : 2 * mm});
        }
        {
            var Q0;
            Q0=makeQuery(id+"F2.opExtrude","SWEPT_BODY",BODY,{"disambiguationData":[OSD([sQuery(id+"F1.wireOp",EDGE,"E19"),sQuery(id+"F1.wireOp",EDGE,"E29.0.startCap"),sQuery(id+"F1.wireOp",EDGE,"E29.0.endCap"),sQuery(id+"F1.wireOp",EDGE,"E29.0.left"),sQuery(id+"F1.wireOp",EDGE,"E29.0.right"),sQuery(id+"F1.wireOp",EDGE,"0684a2df-deec-48ac-a5f3-5ce40cc7b113"),sQuery(id+"F1.wireOp",EDGE,"f0eead35-33e0-4c47-9509-9ec6bf54dab1"),sQuery(id+"F1.wireOp",EDGE,"E35"),sQuery(id+"F1.wireOp",EDGE,"E36.MirrorCS"),sQuery(id+"F1.wireOp",EDGE,"E37.MirrorCS"),sQuery(id+"F1.wireOp",EDGE,"E38.MirrorCS"),sQuery(id+"F1.wireOp",EDGE,"E39.MirrorCS"),sQuery(id+"F1.wireOp",EDGE,"E40"),sQuery(id+"F1.wireOp",EDGE,"E41"),sQuery(id+"F1.wireOp",EDGE,"E90"),sQuery(id+"F1.wireOp",EDGE,"E91")])]});
            var Q1;
            Q1=qCreatedBy(makeId("Right.planeOp"),FACE);
            mirror(context, id + "F14", {"entities" : qUnion([Q0]), "mirrorPlane" : qUnion([Q1])});
        }
        {
            var Q0;
            Q0=makeQuery(id+"F2.opExtrude","SWEPT_BODY",BODY,{"disambiguationData":[OSD([sQuery(id+"F1.wireOp",EDGE,"E19"),sQuery(id+"F1.wireOp",EDGE,"E29.0.startCap"),sQuery(id+"F1.wireOp",EDGE,"E29.0.endCap"),sQuery(id+"F1.wireOp",EDGE,"E29.0.left"),sQuery(id+"F1.wireOp",EDGE,"E29.0.right"),sQuery(id+"F1.wireOp",EDGE,"0684a2df-deec-48ac-a5f3-5ce40cc7b113"),sQuery(id+"F1.wireOp",EDGE,"f0eead35-33e0-4c47-9509-9ec6bf54dab1"),sQuery(id+"F1.wireOp",EDGE,"E35"),sQuery(id+"F1.wireOp",EDGE,"E36.MirrorCS"),sQuery(id+"F1.wireOp",EDGE,"E37.MirrorCS"),sQuery(id+"F1.wireOp",EDGE,"E38.MirrorCS"),sQuery(id+"F1.wireOp",EDGE,"E39.MirrorCS"),sQuery(id+"F1.wireOp",EDGE,"E40"),sQuery(id+"F1.wireOp",EDGE,"E41"),sQuery(id+"F1.wireOp",EDGE,"E90"),sQuery(id+"F1.wireOp",EDGE,"E91")])]});
            var Q1;
            Q1=makeQuery(id+"F14.opPattern","COPY",BODY,{"derivedFrom":makeQuery(id+"F2.opExtrude","SWEPT_BODY",BODY,{"disambiguationData":[OSD([sQuery(id+"F1.wireOp",EDGE,"E19"),sQuery(id+"F1.wireOp",EDGE,"E29.0.startCap"),sQuery(id+"F1.wireOp",EDGE,"E29.0.endCap"),sQuery(id+"F1.wireOp",EDGE,"E29.0.left"),sQuery(id+"F1.wireOp",EDGE,"E29.0.right"),sQuery(id+"F1.wireOp",EDGE,"0684a2df-deec-48ac-a5f3-5ce40cc7b113"),sQuery(id+"F1.wireOp",EDGE,"f0eead35-33e0-4c47-9509-9ec6bf54dab1"),sQuery(id+"F1.wireOp",EDGE,"E35"),sQuery(id+"F1.wireOp",EDGE,"E36.MirrorCS"),sQuery(id+"F1.wireOp",EDGE,"E37.MirrorCS"),sQuery(id+"F1.wireOp",EDGE,"E38.MirrorCS"),sQuery(id+"F1.wireOp",EDGE,"E39.MirrorCS"),sQuery(id+"F1.wireOp",EDGE,"E40"),sQuery(id+"F1.wireOp",EDGE,"E41"),sQuery(id+"F1.wireOp",EDGE,"E90"),sQuery(id+"F1.wireOp",EDGE,"E91")])]}),"instanceName":"1"});
            var Q2;
            Q2=qCreatedBy(makeId("Front.planeOp"),FACE);
            mirror(context, id + "F15", {"entities" : qUnion([Q0, Q1]), "mirrorPlane" : qUnion([Q2])});
        }
    });
